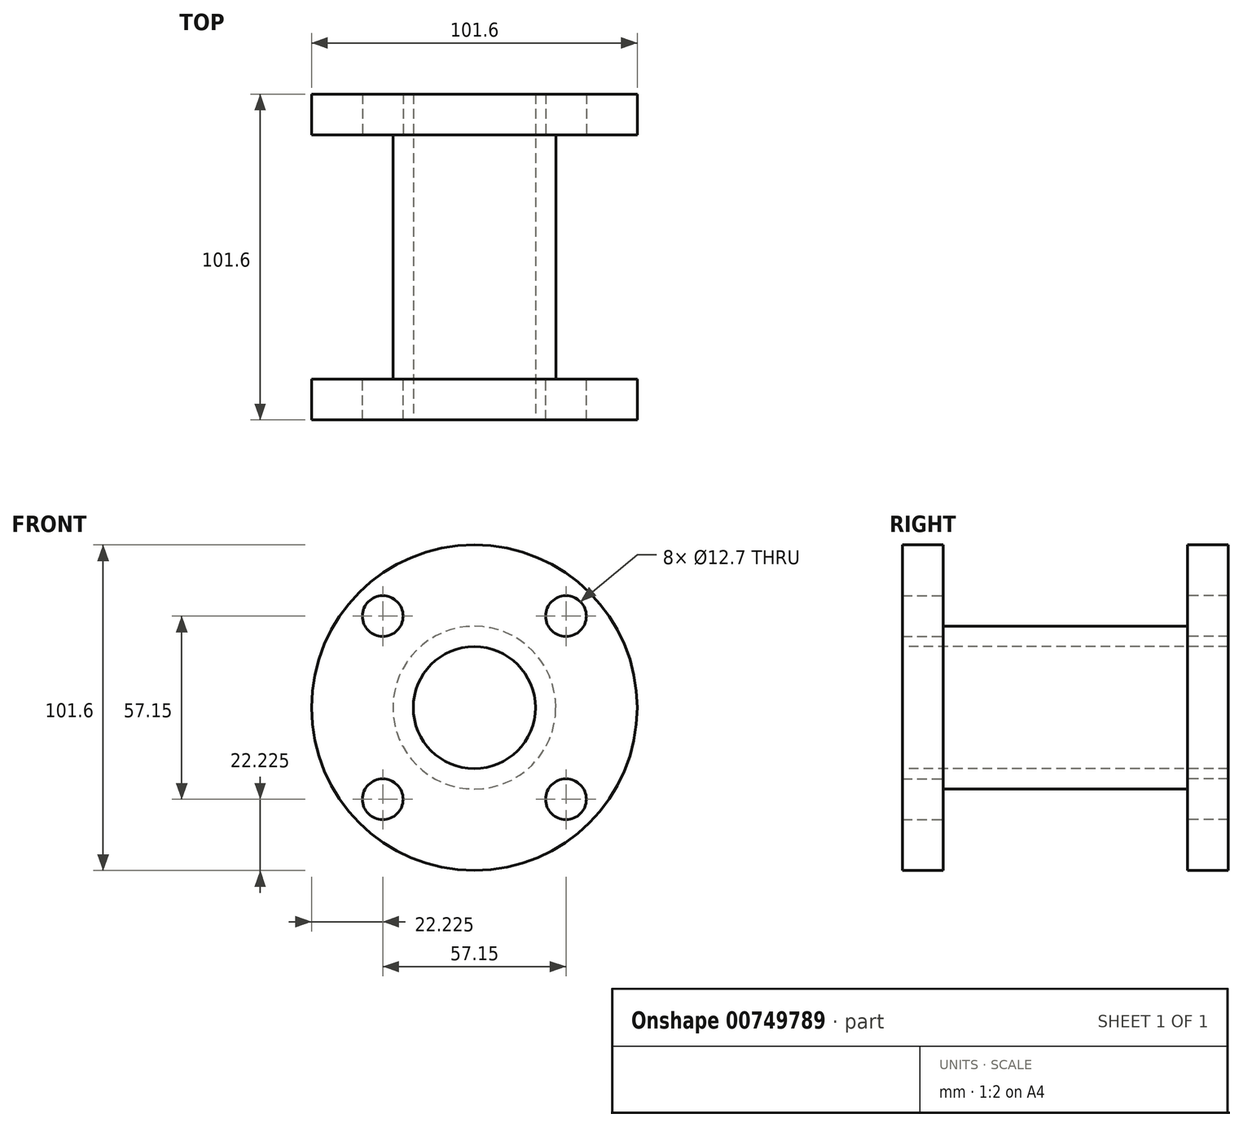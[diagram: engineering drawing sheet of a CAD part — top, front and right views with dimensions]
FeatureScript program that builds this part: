
annotation { "Feature Type Name" : "Feature", "Feature Type Description" : "" }
export const myFeature = defineFeature(function(context is Context, id is Id, definition is map)
    precondition{}
    {
        {
            var Q0;
            Q0=qCreatedBy(makeId("Front.planeOp"),FACE);
            var sketch = newSketch(context, id + "F0", { "sketchPlane" : qUnion([Q0])});
            skCircle(sketch, "E0", {"center": v(0, 0) * mm, "radius": 25.4 * mm});
            skSolve(sketch);
        }
        {
            var Q0;
            Q0 = qSketchRegion(id + "F0", true);
            extrude(context, id + "F1", {"entities" : qUnion([Q0]), "depth" : 76.2 * mm, "offsetDistance" : 25.4 * mm});
        }
        {
            var Q0;
            Q0=makeQuery(id+"F1.opExtrude","CAP_FACE",FACE,{"disambiguationData":[OSD([sQuery(id+"F0.wireOp",EDGE,"E0")])],"isStart":false});
            var sketch = newSketch(context, id + "F2", { "sketchPlane" : qUnion([Q0])});
            skCircle(sketch, "E1", {"center": v(0, 0) * mm, "radius": 50.8 * mm});
            skLineSegment(sketch, "E2.bottom", {"start": v(28.58, 28.58) * mm, "end": v(-28.58, 28.58) * mm, "construction": true});
            skLineSegment(sketch, "E2.top", {"start": v(28.57, -28.58) * mm, "end": v(-28.58, -28.58) * mm, "construction": true});
            skLineSegment(sketch, "E2.left", {"start": v(28.58, 28.58) * mm, "end": v(28.57, -28.58) * mm, "construction": true});
            skLineSegment(sketch, "E2.right", {"start": v(-28.58, 28.58) * mm, "end": v(-28.58, -28.58) * mm, "construction": true});
            skCircle(sketch, "E3", {"center": v(-28.58, 28.58) * mm, "radius": 6.35 * mm});
            skCircle(sketch, "E4", {"center": v(28.58, 28.58) * mm, "radius": 6.35 * mm});
            skCircle(sketch, "E5", {"center": v(28.57, -28.58) * mm, "radius": 6.35 * mm});
            skCircle(sketch, "E6", {"center": v(-28.58, -28.58) * mm, "radius": 6.35 * mm});
            skSolve(sketch);
        }
        {
            var Q0;
            Q0 = qSketchRegion(id + "F2", true);
            extrude(context, id + "F3", {"entities" : qUnion([Q0]), "operationType" : NewBodyOperationType.ADD, "depth" : 12.7 * mm, "offsetDistance" : 25.4 * mm});
        }
        {
            var Q0;
            Q0=makeQuery(id+"F3.opExtrude","CAP_FACE",FACE,{"disambiguationData":[OSD([sQuery(id+"F2.wireOp",EDGE,"E1"),sQuery(id+"F2.wireOp",EDGE,"E3"),sQuery(id+"F2.wireOp",EDGE,"E4"),sQuery(id+"F2.wireOp",EDGE,"E5"),sQuery(id+"F2.wireOp",EDGE,"E6")])],"isStart":false});
            var sketch = newSketch(context, id + "F4", { "sketchPlane" : qUnion([Q0])});
            skCircle(sketch, "E7", {"center": v(0, 0) * mm, "radius": 19.05 * mm});
            skSolve(sketch);
        }
        {
            var Q0;
            Q0=makeQuery(id+"F1.opExtrude","CAP_FACE",FACE,{"disambiguationData":[OSD([sQuery(id+"F0.wireOp",EDGE,"E0")])],"isStart":true});
            var sketch = newSketch(context, id + "F5", { "sketchPlane" : qUnion([Q0])});
            skLineSegment(sketch, "E8.bottom", {"start": v(28.58, 28.58) * mm, "end": v(-28.58, 28.58) * mm, "construction": true});
            skLineSegment(sketch, "E8.top", {"start": v(28.58, -28.58) * mm, "end": v(-28.58, -28.58) * mm, "construction": true});
            skLineSegment(sketch, "E8.left", {"start": v(28.58, 28.58) * mm, "end": v(28.58, -28.58) * mm, "construction": true});
            skLineSegment(sketch, "E8.right", {"start": v(-28.57, 28.58) * mm, "end": v(-28.58, -28.58) * mm, "construction": true});
            skPoint(sketch, "E8.middle", {"position": v(0, 0) * mm});
            skCircle(sketch, "E9", {"center": v(-28.58, 28.58) * mm, "radius": 6.35 * mm});
            skCircle(sketch, "E10", {"center": v(28.58, 28.58) * mm, "radius": 6.35 * mm});
            skCircle(sketch, "E11", {"center": v(28.58, -28.58) * mm, "radius": 6.35 * mm});
            skCircle(sketch, "E12", {"center": v(-28.58, -28.58) * mm, "radius": 6.35 * mm});
            skCircle(sketch, "E13", {"center": v(0, 0) * mm, "radius": 50.8 * mm});
            skSolve(sketch);
        }
        {
            var Q0;
            Q0 = qSketchRegion(id + "F5", true);
            extrude(context, id + "F6", {"entities" : qUnion([Q0]), "operationType" : NewBodyOperationType.ADD, "depth" : 12.7 * mm, "offsetDistance" : 25.4 * mm});
        }
        {
            var Q0;
            Q0 = qSketchRegion(id + "F4", true);
            extrude(context, id + "F7", {"entities" : qUnion([Q0]), "operationType" : NewBodyOperationType.REMOVE, "oppositeDirection" : true, "depth" : 137.92 * mm, "offsetDistance" : 25.4 * mm});
        }
    });
